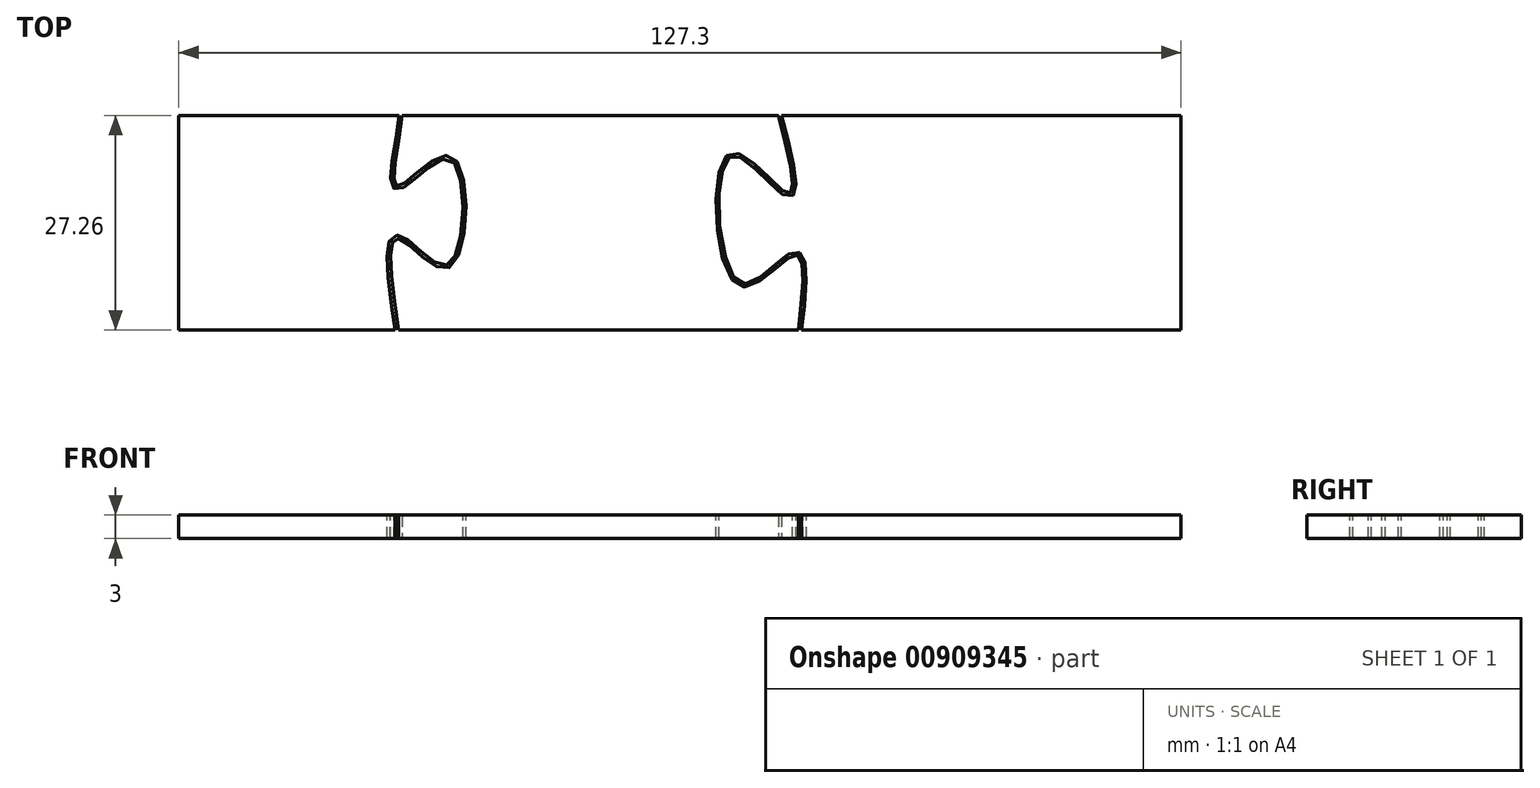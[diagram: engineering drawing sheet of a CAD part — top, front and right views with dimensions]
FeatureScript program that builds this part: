
annotation { "Feature Type Name" : "Feature", "Feature Type Description" : "" }
export const myFeature = defineFeature(function(context is Context, id is Id, definition is map)
    precondition{}
    {
        {
            var Q0;
            Q0=qCreatedBy(makeId("Top.planeOp"),FACE);
            var sketch = newSketch(context, id + "F0", { "sketchPlane" : qUnion([Q0])});
            skLineSegment(sketch, "E0.bottom", {"start": v(63.65, 13.63) * mm, "end": v(-63.65, 13.63) * mm});
            skLineSegment(sketch, "E0.top", {"start": v(63.65, -13.63) * mm, "end": v(-63.65, -13.63) * mm});
            skLineSegment(sketch, "E0.left", {"start": v(63.65, 13.63) * mm, "end": v(63.65, -13.63) * mm});
            skLineSegment(sketch, "E0.right", {"start": v(-63.65, 13.63) * mm, "end": v(-63.65, -13.63) * mm});
            skPoint(sketch, "E0.middle", {"position": v(0, 0) * mm});
            skFitSpline(sketch, "E1", {"points": [v(-35.28, 13.63) * mm, v(-35.67, 4.63) * mm, v(-28.96, 8.38) * mm, v(-29.3, -5.7) * mm, v(-35.74, -2.03) * mm, v(-35.74, -13.63) * mm], "startDerivative": vector(-9.18, -79.4) * mm, "endDerivative": vector(12.6, -84.16) * mm});
            skFitSpline(sketch, "E2", {"points": [v(12.52, 13.63) * mm, v(13.67, 3.72) * mm, v(6.31, 8.77) * mm, v(7.46, -8) * mm, v(14.59, -4.1) * mm, v(15.05, -13.63) * mm], "startDerivative": vector(20.26, -80.02) * mm, "endDerivative": vector(-9.23, -77.37) * mm});
            skFitSpline(sketch, "E3.0", {"points": [v(-35.68, 13.67) * mm, v(-35.77, 12.85) * mm, v(-36, 11.24) * mm, v(-36.28, 9.41) * mm, v(-36.48, 8.1) * mm, v(-36.6, 7.22) * mm, v(-36.69, 6.42) * mm, v(-36.73, 5.74) * mm, v(-36.7, 5.27) * mm, v(-36.64, 4.93) * mm, v(-36.57, 4.7) * mm, v(-36.44, 4.48) * mm, v(-36.23, 4.3) * mm, v(-35.96, 4.2) * mm, v(-35.69, 4.2) * mm, v(-35.44, 4.28) * mm, v(-35.2, 4.4) * mm, v(-34.95, 4.54) * mm, v(-34.61, 4.78) * mm, v(-34.15, 5.15) * mm, v(-33.55, 5.66) * mm, v(-32.92, 6.21) * mm, v(-32.26, 6.76) * mm, v(-31.6, 7.27) * mm, v(-30.94, 7.7) * mm, v(-30.33, 8) * mm, v(-29.79, 8.15) * mm, v(-29.36, 8.13) * mm, v(-29.02, 7.97) * mm, v(-28.65, 7.58) * mm, v(-28.32, 6.95) * mm, v(-28.04, 6.12) * mm, v(-27.75, 4.82) * mm, v(-27.55, 2.9) * mm, v(-27.58, 0.42) * mm, v(-27.82, -1.56) * mm, v(-28.13, -2.95) * mm, v(-28.42, -3.86) * mm, v(-28.76, -4.6) * mm, v(-29.08, -5.03) * mm, v(-29.33, -5.25) * mm, v(-29.5, -5.36) * mm, v(-29.68, -5.42) * mm, v(-29.94, -5.46) * mm, v(-30.33, -5.4) * mm, v(-30.89, -5.16) * mm, v(-31.5, -4.78) * mm, v(-32.12, -4.3) * mm, v(-32.75, -3.77) * mm, v(-33.38, -3.22) * mm, v(-33.98, -2.7) * mm, v(-34.55, -2.22) * mm, v(-35, -1.91) * mm, v(-35.34, -1.73) * mm, v(-35.6, -1.64) * mm, v(-35.9, -1.6) * mm, v(-36.17, -1.63) * mm, v(-36.43, -1.75) * mm, v(-36.64, -1.93) * mm, v(-36.8, -2.16) * mm, v(-36.95, -2.49) * mm, v(-37.08, -2.96) * mm, v(-37.16, -3.65) * mm, v(-37.18, -4.45) * mm, v(-37.16, -5.36) * mm, v(-37.07, -6.7) * mm, v(-36.87, -8.57) * mm, v(-36.53, -11.06) * mm, v(-36.27, -12.8) * mm, v(-36.13, -13.68) * mm]});
            skFitSpline(sketch, "E4.0", {"points": [v(12.9, 13.72) * mm, v(13.12, 12.9) * mm, v(13.54, 11.22) * mm, v(14.01, 9.25) * mm, v(14.32, 7.8) * mm, v(14.5, 6.8) * mm, v(14.65, 5.91) * mm, v(14.72, 5.13) * mm, v(14.73, 4.58) * mm, v(14.7, 4.2) * mm, v(14.63, 3.93) * mm, v(14.53, 3.69) * mm, v(14.37, 3.47) * mm, v(14.1, 3.3) * mm, v(13.8, 3.27) * mm, v(13.53, 3.33) * mm, v(13.28, 3.45) * mm, v(13.03, 3.61) * mm, v(12.68, 3.88) * mm, v(12.2, 4.3) * mm, v(11.6, 4.9) * mm, v(10.93, 5.56) * mm, v(10.23, 6.25) * mm, v(9.52, 6.92) * mm, v(8.82, 7.52) * mm, v(8.14, 8.02) * mm, v(7.51, 8.36) * mm, v(7.06, 8.5) * mm, v(6.78, 8.5) * mm, v(6.6, 8.46) * mm, v(6.42, 8.39) * mm, v(6.25, 8.25) * mm, v(6.07, 8.05) * mm, v(5.84, 7.69) * mm, v(5.58, 7.08) * mm, v(5.32, 6.13) * mm, v(5.14, 5.02) * mm, v(4.98, 3.37) * mm, v(4.97, 1.08) * mm, v(5.22, -1.73) * mm, v(5.65, -3.9) * mm, v(6.11, -5.37) * mm, v(6.5, -6.32) * mm, v(6.95, -7.05) * mm, v(7.34, -7.46) * mm, v(7.64, -7.65) * mm, v(7.94, -7.77) * mm, v(8.34, -7.8) * mm, v(8.92, -7.65) * mm, v(9.57, -7.34) * mm, v(10.24, -6.9) * mm, v(10.94, -6.36) * mm, v(11.62, -5.78) * mm, v(12.29, -5.2) * mm, v(12.92, -4.65) * mm, v(13.42, -4.26) * mm, v(13.8, -4) * mm, v(14.07, -3.85) * mm, v(14.35, -3.73) * mm, v(14.64, -3.67) * mm, v(14.93, -3.69) * mm, v(15.21, -3.79) * mm, v(15.44, -3.97) * mm, v(15.61, -4.19) * mm, v(15.74, -4.44) * mm, v(15.88, -4.81) * mm, v(15.98, -5.35) * mm, v(16.05, -6.11) * mm, v(16.06, -6.98) * mm, v(16.02, -7.95) * mm, v(15.93, -9.34) * mm, v(15.73, -11.25) * mm, v(15.54, -12.87) * mm, v(15.44, -13.67) * mm]});
            skSolve(sketch);
        }
        {
            var Q0;
            {var subQ0=sQuery(id+"F0.wireOp",EDGE,"E2");Q0=makeQuery(id+"F0.imprint","IMPRINT",FACE,{"disambiguationData":[TD([[makeQuery(id+"F0.imprint","IMPRINT",EDGE,{"derivedFrom":subQ0}),1.0]])]});}
            var Q1;
            {var subQ0=sQuery(id+"F0.wireOp",EDGE,"E0.left");Q1=makeQuery(id+"F0.imprint","IMPRINT",FACE,{"disambiguationData":[TD([[makeQuery(id+"F0.imprint","IMPRINT",EDGE,{"derivedFrom":subQ0}),-1.0]])]});}
            var Q2;
            {var subQ0=sQuery(id+"F0.wireOp",EDGE,"E1");Q2=makeQuery(id+"F0.imprint","IMPRINT",FACE,{"disambiguationData":[TD([[makeQuery(id+"F0.imprint","IMPRINT",EDGE,{"derivedFrom":subQ0}),1.0]])]});}
            var Q3;
            {var subQ0=sQuery(id+"F0.wireOp",EDGE,"E1");Q3=makeQuery(id+"F0.imprint","IMPRINT",FACE,{"disambiguationData":[TD([[makeQuery(id+"F0.imprint","IMPRINT",EDGE,{"derivedFrom":subQ0}),-1.0]])]});}
            var Q4;
            {var subQ0=sQuery(id+"F0.wireOp",EDGE,"E0.right");Q4=makeQuery(id+"F0.imprint","IMPRINT",FACE,{"disambiguationData":[TD([[makeQuery(id+"F0.imprint","IMPRINT",EDGE,{"derivedFrom":subQ0}),1.0]])]});}
            extrude(context, id + "F1", {"entities" : qUnion([Q0, Q1, Q2, Q3, Q4]), "depth" : 3 * mm, "offsetDistance" : 25 * mm});
        }
        {
            var Q0;
            {var subQ0=sQuery(id+"F0.wireOp",EDGE,"E1");Q0=makeQuery(id+"F0.imprint","IMPRINT",FACE,{"disambiguationData":[TD([[makeQuery(id+"F0.imprint","IMPRINT",EDGE,{"derivedFrom":subQ0}),-1.0]])]});}
            var Q1;
            {var subQ0=sQuery(id+"F0.wireOp",EDGE,"E2");Q1=makeQuery(id+"F0.imprint","IMPRINT",FACE,{"disambiguationData":[TD([[makeQuery(id+"F0.imprint","IMPRINT",EDGE,{"derivedFrom":subQ0}),1.0]])]});}
            extrude(context, id + "F2", {"entities" : qUnion([Q0, Q1]), "operationType" : NewBodyOperationType.REMOVE, "depth" : 25 * mm, "offsetDistance" : 25 * mm});
        }
    });
